# Revit family: SVC-4-22D_GENERADO
name_source: partatom
category: Equipos especializados
units: mm (PartAtom-declared; Revit-internal decimal feet)

## family parameters
Compartido = No
Corte con vacíos al cargar = No
Cota de conector redondo = Diámetro de uso
Punto de cálculo de habitación = No
Se basa en plano de trabajo = No
Siempre vertical = Sí
Tipo de pieza = Normal

## types (2) — shared parameters
Comentarios de tipo = Two tanks of 22 and 4 litres capacity.
Cycle = 50 Hz
Depth = 332 mm  [stored 1.08924 ft]
Fabricante = SAMMIC S.L.
Foodservice Equipment Identifier = Sí
HP = 2.55
Height = 290 mm  [stored 0.951444 ft]
Phase = 1
Revision Code = 1
Specification by Manufacturer = Unstirred sous-vide digital bath.
URL = https://www.sammic.com
URL Cutsheet = http://www.sammic.com
Volts = 230 V
Watts = 1900 W
Weight in Pounds = 36.6
Width = 716 mm  [stored 2.34908 ft]
zero-valued in all types: Elevación por defecto

## per-type parameters (varying)
| type | Conn Plug | Modelo |
| Sous-vide SVC4-22D  230/50-60/1 | EU | 5170010 |
| Sous-vide cooker SVC-4-22D 230/50-60/1 UK | UK | 5170013 |

note: column(s) folded — value = type name in every type: Descripción

note: [stored X ft] marks values corroborated as IEEE doubles in the binary element streams (Revit-internal decimal feet)
